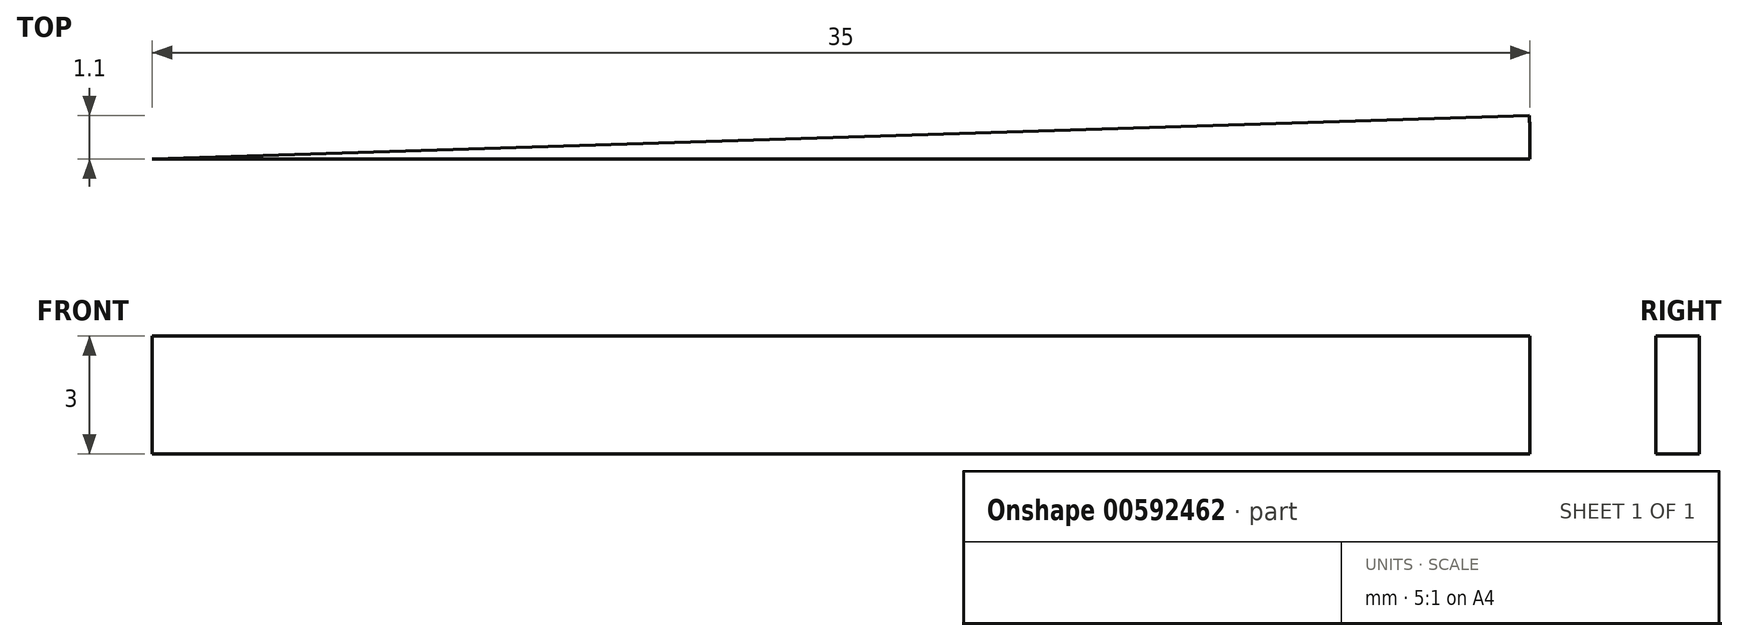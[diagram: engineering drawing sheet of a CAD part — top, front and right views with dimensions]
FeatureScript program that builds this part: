
annotation { "Feature Type Name" : "Feature", "Feature Type Description" : "" }
export const myFeature = defineFeature(function(context is Context, id is Id, definition is map)
    precondition{}
    {
        {
            var Q0;
            Q0=qCreatedBy(makeId("Top.planeOp"),FACE);
            var sketch = newSketch(context, id + "F0", { "sketchPlane" : qUnion([Q0])});
            skCircle(sketch, "E0", {"center": v(0, 0) * mm, "radius": 35 * mm});
            skLineSegment(sketch, "E1", {"start": v(0, 0) * mm, "end": v(35, 0) * mm});
            skLineSegment(sketch, "E2.1.0", {"start": v(0, 0) * mm, "end": v(34.98, 1.1) * mm});
            skLineSegment(sketch, "E3.1.2.0", {"start": v(0, 0) * mm, "end": v(34.93, 2.2) * mm});
            skLineSegment(sketch, "E3.1.3.0", {"start": v(0, 0) * mm, "end": v(34.84, 3.3) * mm});
            skLineSegment(sketch, "E3.1.4.0", {"start": v(0, 0) * mm, "end": v(34.72, 4.39) * mm});
            skLineSegment(sketch, "E3.1.5.0", {"start": v(0, 0) * mm, "end": v(34.57, 5.48) * mm});
            skLineSegment(sketch, "E3.1.6.0", {"start": v(0, 0) * mm, "end": v(34.38, 6.56) * mm});
            skLineSegment(sketch, "E4.1.7.0", {"start": v(0, 0) * mm, "end": v(34.16, 7.64) * mm});
            skLineSegment(sketch, "E5.1.8.0", {"start": v(0, 0) * mm, "end": v(33.9, 8.7) * mm});
            skLineSegment(sketch, "E6.1.9.0", {"start": v(0, 0) * mm, "end": v(33.61, 9.76) * mm});
            skLineSegment(sketch, "E7.1.10.0", {"start": v(0, 0) * mm, "end": v(33.29, 10.82) * mm});
            skLineSegment(sketch, "E8.1.11.0", {"start": v(0, 0) * mm, "end": v(32.93, 11.86) * mm});
            skLineSegment(sketch, "E9.1.12.0", {"start": v(0, 0) * mm, "end": v(32.54, 12.88) * mm});
            skLineSegment(sketch, "E9.1.13.0", {"start": v(0, 0) * mm, "end": v(32.12, 13.9) * mm});
            skLineSegment(sketch, "E9.1.14.0", {"start": v(0, 0) * mm, "end": v(31.67, 14.9) * mm});
            skLineSegment(sketch, "E9.1.15.0", {"start": v(0, 0) * mm, "end": v(31.19, 15.89) * mm});
            skLineSegment(sketch, "E9.1.16.0", {"start": v(0, 0) * mm, "end": v(30.67, 16.86) * mm});
            skLineSegment(sketch, "E9.1.17.0", {"start": v(0, 0) * mm, "end": v(30.13, 17.82) * mm});
            skLineSegment(sketch, "E9.1.18.0", {"start": v(0, 0) * mm, "end": v(29.55, 18.75) * mm});
            skLineSegment(sketch, "E9.1.19.0", {"start": v(0, 0) * mm, "end": v(28.95, 19.67) * mm});
            skLineSegment(sketch, "E9.1.20.0", {"start": v(0, 0) * mm, "end": v(28.32, 20.57) * mm});
            skLineSegment(sketch, "E9.1.21.0", {"start": v(0, 0) * mm, "end": v(27.66, 21.45) * mm});
            skLineSegment(sketch, "E9.1.22.0", {"start": v(0, 0) * mm, "end": v(26.97, 22.3) * mm});
            skLineSegment(sketch, "E9.1.23.0", {"start": v(0, 0) * mm, "end": v(26.25, 23.15) * mm});
            skLineSegment(sketch, "E9.1.24.0", {"start": v(0, 0) * mm, "end": v(25.51, 23.96) * mm});
            skLineSegment(sketch, "E9.1.25.0", {"start": v(0, 0) * mm, "end": v(24.75, 24.75) * mm});
            skLineSegment(sketch, "E9.1.26.0", {"start": v(0, 0) * mm, "end": v(23.96, 25.51) * mm});
            skLineSegment(sketch, "E9.1.27.0", {"start": v(0, 0) * mm, "end": v(23.15, 26.25) * mm});
            skLineSegment(sketch, "E9.1.28.0", {"start": v(0, 0) * mm, "end": v(22.3, 26.97) * mm});
            skLineSegment(sketch, "E9.1.29.0", {"start": v(0, 0) * mm, "end": v(21.45, 27.66) * mm});
            skLineSegment(sketch, "E9.1.30.0", {"start": v(0, 0) * mm, "end": v(20.57, 28.32) * mm});
            skLineSegment(sketch, "E9.1.31.0", {"start": v(0, 0) * mm, "end": v(19.67, 28.95) * mm});
            skLineSegment(sketch, "E9.1.32.0", {"start": v(0, 0) * mm, "end": v(18.75, 29.55) * mm});
            skLineSegment(sketch, "E9.1.33.0", {"start": v(0, 0) * mm, "end": v(17.82, 30.13) * mm});
            skLineSegment(sketch, "E9.1.34.0", {"start": v(0, 0) * mm, "end": v(16.86, 30.67) * mm});
            skLineSegment(sketch, "E9.1.35.0", {"start": v(0, 0) * mm, "end": v(15.89, 31.19) * mm});
            skLineSegment(sketch, "E9.1.36.0", {"start": v(0, 0) * mm, "end": v(14.9, 31.67) * mm});
            skLineSegment(sketch, "E9.1.37.0", {"start": v(0, 0) * mm, "end": v(13.9, 32.12) * mm});
            skLineSegment(sketch, "E9.1.38.0", {"start": v(0, 0) * mm, "end": v(12.88, 32.54) * mm});
            skLineSegment(sketch, "E9.1.39.0", {"start": v(0, 0) * mm, "end": v(11.86, 32.93) * mm});
            skLineSegment(sketch, "E9.1.40.0", {"start": v(0, 0) * mm, "end": v(10.82, 33.29) * mm});
            skLineSegment(sketch, "E9.1.41.0", {"start": v(0, 0) * mm, "end": v(9.76, 33.61) * mm});
            skLineSegment(sketch, "E9.1.42.0", {"start": v(0, 0) * mm, "end": v(8.7, 33.9) * mm});
            skLineSegment(sketch, "E9.1.43.0", {"start": v(0, 0) * mm, "end": v(7.64, 34.16) * mm});
            skLineSegment(sketch, "E9.1.44.0", {"start": v(0, 0) * mm, "end": v(6.56, 34.38) * mm});
            skLineSegment(sketch, "E9.1.45.0", {"start": v(0, 0) * mm, "end": v(5.48, 34.57) * mm});
            skLineSegment(sketch, "E9.1.46.0", {"start": v(0, 0) * mm, "end": v(4.39, 34.72) * mm});
            skLineSegment(sketch, "E9.1.47.0", {"start": v(0, 0) * mm, "end": v(3.3, 34.84) * mm});
            skLineSegment(sketch, "E9.1.48.0", {"start": v(0, 0) * mm, "end": v(2.2, 34.93) * mm});
            skLineSegment(sketch, "E9.1.49.0", {"start": v(0, 0) * mm, "end": v(1.1, 34.98) * mm});
            skLineSegment(sketch, "E9.1.50.0", {"start": v(0, 0) * mm, "end": v(0, 35) * mm});
            skLineSegment(sketch, "E9.1.51.0", {"start": v(0, 0) * mm, "end": v(-1.1, 34.98) * mm});
            skLineSegment(sketch, "E9.1.52.0", {"start": v(0, 0) * mm, "end": v(-2.2, 34.93) * mm});
            skLineSegment(sketch, "E9.1.53.0", {"start": v(0, 0) * mm, "end": v(-3.3, 34.84) * mm});
            skLineSegment(sketch, "E9.1.54.0", {"start": v(0, 0) * mm, "end": v(-4.39, 34.72) * mm});
            skLineSegment(sketch, "E9.1.55.0", {"start": v(0, 0) * mm, "end": v(-5.48, 34.57) * mm});
            skLineSegment(sketch, "E9.1.56.0", {"start": v(0, 0) * mm, "end": v(-6.56, 34.38) * mm});
            skLineSegment(sketch, "E9.1.57.0", {"start": v(0, 0) * mm, "end": v(-7.64, 34.16) * mm});
            skLineSegment(sketch, "E9.1.58.0", {"start": v(0, 0) * mm, "end": v(-8.7, 33.9) * mm});
            skLineSegment(sketch, "E9.1.59.0", {"start": v(0, 0) * mm, "end": v(-9.76, 33.61) * mm});
            skLineSegment(sketch, "E9.1.60.0", {"start": v(0, 0) * mm, "end": v(-10.82, 33.29) * mm});
            skLineSegment(sketch, "E9.1.61.0", {"start": v(0, 0) * mm, "end": v(-11.86, 32.93) * mm});
            skLineSegment(sketch, "E9.1.62.0", {"start": v(0, 0) * mm, "end": v(-12.88, 32.54) * mm});
            skLineSegment(sketch, "E9.1.63.0", {"start": v(0, 0) * mm, "end": v(-13.9, 32.12) * mm});
            skLineSegment(sketch, "E9.1.64.0", {"start": v(0, 0) * mm, "end": v(-14.9, 31.67) * mm});
            skLineSegment(sketch, "E9.1.65.0", {"start": v(0, 0) * mm, "end": v(-15.89, 31.19) * mm});
            skLineSegment(sketch, "E9.1.66.0", {"start": v(0, 0) * mm, "end": v(-16.86, 30.67) * mm});
            skLineSegment(sketch, "E9.1.67.0", {"start": v(0, 0) * mm, "end": v(-17.82, 30.13) * mm});
            skLineSegment(sketch, "E9.1.68.0", {"start": v(0, 0) * mm, "end": v(-18.75, 29.55) * mm});
            skLineSegment(sketch, "E9.1.69.0", {"start": v(0, 0) * mm, "end": v(-19.67, 28.95) * mm});
            skLineSegment(sketch, "E9.1.70.0", {"start": v(0, 0) * mm, "end": v(-20.57, 28.32) * mm});
            skLineSegment(sketch, "E9.1.71.0", {"start": v(0, 0) * mm, "end": v(-21.45, 27.66) * mm});
            skLineSegment(sketch, "E9.1.72.0", {"start": v(0, 0) * mm, "end": v(-22.3, 26.97) * mm});
            skLineSegment(sketch, "E9.1.73.0", {"start": v(0, 0) * mm, "end": v(-23.15, 26.25) * mm});
            skLineSegment(sketch, "E9.1.74.0", {"start": v(0, 0) * mm, "end": v(-23.96, 25.51) * mm});
            skLineSegment(sketch, "E9.1.75.0", {"start": v(0, 0) * mm, "end": v(-24.75, 24.75) * mm});
            skLineSegment(sketch, "E9.1.76.0", {"start": v(0, 0) * mm, "end": v(-25.51, 23.96) * mm});
            skLineSegment(sketch, "E9.1.77.0", {"start": v(0, 0) * mm, "end": v(-26.25, 23.15) * mm});
            skLineSegment(sketch, "E9.1.78.0", {"start": v(0, 0) * mm, "end": v(-26.97, 22.3) * mm});
            skLineSegment(sketch, "E9.1.79.0", {"start": v(0, 0) * mm, "end": v(-27.66, 21.45) * mm});
            skLineSegment(sketch, "E9.1.80.0", {"start": v(0, 0) * mm, "end": v(-28.32, 20.57) * mm});
            skLineSegment(sketch, "E9.1.81.0", {"start": v(0, 0) * mm, "end": v(-28.95, 19.67) * mm});
            skLineSegment(sketch, "E9.1.82.0", {"start": v(0, 0) * mm, "end": v(-29.55, 18.75) * mm});
            skLineSegment(sketch, "E9.1.83.0", {"start": v(0, 0) * mm, "end": v(-30.13, 17.82) * mm});
            skLineSegment(sketch, "E9.1.84.0", {"start": v(0, 0) * mm, "end": v(-30.67, 16.86) * mm});
            skLineSegment(sketch, "E9.1.85.0", {"start": v(0, 0) * mm, "end": v(-31.19, 15.89) * mm});
            skLineSegment(sketch, "E9.1.86.0", {"start": v(0, 0) * mm, "end": v(-31.67, 14.9) * mm});
            skLineSegment(sketch, "E9.1.87.0", {"start": v(0, 0) * mm, "end": v(-32.12, 13.9) * mm});
            skLineSegment(sketch, "E9.1.88.0", {"start": v(0, 0) * mm, "end": v(-32.54, 12.88) * mm});
            skLineSegment(sketch, "E9.1.89.0", {"start": v(0, 0) * mm, "end": v(-32.93, 11.86) * mm});
            skLineSegment(sketch, "E9.1.90.0", {"start": v(0, 0) * mm, "end": v(-33.29, 10.82) * mm});
            skLineSegment(sketch, "E9.1.91.0", {"start": v(0, 0) * mm, "end": v(-33.61, 9.76) * mm});
            skLineSegment(sketch, "E9.1.92.0", {"start": v(0, 0) * mm, "end": v(-33.9, 8.7) * mm});
            skLineSegment(sketch, "E9.1.93.0", {"start": v(0, 0) * mm, "end": v(-34.16, 7.64) * mm});
            skLineSegment(sketch, "E9.1.94.0", {"start": v(0, 0) * mm, "end": v(-34.38, 6.56) * mm});
            skLineSegment(sketch, "E9.1.95.0", {"start": v(0, 0) * mm, "end": v(-34.57, 5.48) * mm});
            skLineSegment(sketch, "E9.1.96.0", {"start": v(0, 0) * mm, "end": v(-34.72, 4.39) * mm});
            skLineSegment(sketch, "E9.1.97.0", {"start": v(0, 0) * mm, "end": v(-34.84, 3.3) * mm});
            skLineSegment(sketch, "E9.1.98.0", {"start": v(0, 0) * mm, "end": v(-34.93, 2.2) * mm});
            skLineSegment(sketch, "E9.1.99.0", {"start": v(0, 0) * mm, "end": v(-34.98, 1.1) * mm});
            skLineSegment(sketch, "E9.1.100.0", {"start": v(0, 0) * mm, "end": v(-35, 0) * mm});
            skLineSegment(sketch, "E9.1.101.0", {"start": v(0, 0) * mm, "end": v(-34.98, -1.1) * mm});
            skLineSegment(sketch, "E9.1.102.0", {"start": v(0, 0) * mm, "end": v(-34.93, -2.2) * mm});
            skLineSegment(sketch, "E9.1.103.0", {"start": v(0, 0) * mm, "end": v(-34.84, -3.3) * mm});
            skLineSegment(sketch, "E9.1.104.0", {"start": v(0, 0) * mm, "end": v(-34.72, -4.39) * mm});
            skLineSegment(sketch, "E9.1.105.0", {"start": v(0, 0) * mm, "end": v(-34.57, -5.48) * mm});
            skLineSegment(sketch, "E9.1.106.0", {"start": v(0, 0) * mm, "end": v(-34.38, -6.56) * mm});
            skLineSegment(sketch, "E9.1.107.0", {"start": v(0, 0) * mm, "end": v(-34.16, -7.64) * mm});
            skLineSegment(sketch, "E9.1.108.0", {"start": v(0, 0) * mm, "end": v(-33.9, -8.7) * mm});
            skLineSegment(sketch, "E9.1.109.0", {"start": v(0, 0) * mm, "end": v(-33.61, -9.76) * mm});
            skLineSegment(sketch, "E9.1.110.0", {"start": v(0, 0) * mm, "end": v(-33.29, -10.82) * mm});
            skLineSegment(sketch, "E9.1.111.0", {"start": v(0, 0) * mm, "end": v(-32.93, -11.86) * mm});
            skLineSegment(sketch, "E9.1.112.0", {"start": v(0, 0) * mm, "end": v(-32.54, -12.88) * mm});
            skLineSegment(sketch, "E9.1.113.0", {"start": v(0, 0) * mm, "end": v(-32.12, -13.9) * mm});
            skLineSegment(sketch, "E9.1.114.0", {"start": v(0, 0) * mm, "end": v(-31.67, -14.9) * mm});
            skLineSegment(sketch, "E9.1.115.0", {"start": v(0, 0) * mm, "end": v(-31.19, -15.89) * mm});
            skLineSegment(sketch, "E9.1.116.0", {"start": v(0, 0) * mm, "end": v(-30.67, -16.86) * mm});
            skLineSegment(sketch, "E9.1.117.0", {"start": v(0, 0) * mm, "end": v(-30.13, -17.82) * mm});
            skLineSegment(sketch, "E9.1.118.0", {"start": v(0, 0) * mm, "end": v(-29.55, -18.75) * mm});
            skLineSegment(sketch, "E9.1.119.0", {"start": v(0, 0) * mm, "end": v(-28.95, -19.67) * mm});
            skLineSegment(sketch, "E9.1.120.0", {"start": v(0, 0) * mm, "end": v(-28.32, -20.57) * mm});
            skLineSegment(sketch, "E9.1.121.0", {"start": v(0, 0) * mm, "end": v(-27.66, -21.45) * mm});
            skLineSegment(sketch, "E9.1.122.0", {"start": v(0, 0) * mm, "end": v(-26.97, -22.3) * mm});
            skLineSegment(sketch, "E9.1.123.0", {"start": v(0, 0) * mm, "end": v(-26.25, -23.15) * mm});
            skLineSegment(sketch, "E9.1.124.0", {"start": v(0, 0) * mm, "end": v(-25.51, -23.96) * mm});
            skLineSegment(sketch, "E9.1.125.0", {"start": v(0, 0) * mm, "end": v(-24.75, -24.75) * mm});
            skLineSegment(sketch, "E9.1.126.0", {"start": v(0, 0) * mm, "end": v(-23.96, -25.51) * mm});
            skLineSegment(sketch, "E9.1.127.0", {"start": v(0, 0) * mm, "end": v(-23.15, -26.25) * mm});
            skLineSegment(sketch, "E9.1.128.0", {"start": v(0, 0) * mm, "end": v(-22.3, -26.97) * mm});
            skLineSegment(sketch, "E9.1.129.0", {"start": v(0, 0) * mm, "end": v(-21.45, -27.66) * mm});
            skLineSegment(sketch, "E9.1.130.0", {"start": v(0, 0) * mm, "end": v(-20.57, -28.32) * mm});
            skLineSegment(sketch, "E9.1.131.0", {"start": v(0, 0) * mm, "end": v(-19.67, -28.95) * mm});
            skLineSegment(sketch, "E9.1.132.0", {"start": v(0, 0) * mm, "end": v(-18.75, -29.55) * mm});
            skLineSegment(sketch, "E9.1.133.0", {"start": v(0, 0) * mm, "end": v(-17.82, -30.13) * mm});
            skLineSegment(sketch, "E9.1.134.0", {"start": v(0, 0) * mm, "end": v(-16.86, -30.67) * mm});
            skLineSegment(sketch, "E9.1.135.0", {"start": v(0, 0) * mm, "end": v(-15.89, -31.19) * mm});
            skLineSegment(sketch, "E9.1.136.0", {"start": v(0, 0) * mm, "end": v(-14.9, -31.67) * mm});
            skLineSegment(sketch, "E9.1.137.0", {"start": v(0, 0) * mm, "end": v(-13.9, -32.12) * mm});
            skLineSegment(sketch, "E9.1.138.0", {"start": v(0, 0) * mm, "end": v(-12.88, -32.54) * mm});
            skLineSegment(sketch, "E9.1.139.0", {"start": v(0, 0) * mm, "end": v(-11.86, -32.93) * mm});
            skLineSegment(sketch, "E9.1.140.0", {"start": v(0, 0) * mm, "end": v(-10.82, -33.29) * mm});
            skLineSegment(sketch, "E9.1.141.0", {"start": v(0, 0) * mm, "end": v(-9.76, -33.61) * mm});
            skLineSegment(sketch, "E9.1.142.0", {"start": v(0, 0) * mm, "end": v(-8.7, -33.9) * mm});
            skLineSegment(sketch, "E9.1.143.0", {"start": v(0, 0) * mm, "end": v(-7.64, -34.16) * mm});
            skLineSegment(sketch, "E9.1.144.0", {"start": v(0, 0) * mm, "end": v(-6.56, -34.38) * mm});
            skLineSegment(sketch, "E9.1.145.0", {"start": v(0, 0) * mm, "end": v(-5.48, -34.57) * mm});
            skLineSegment(sketch, "E9.1.146.0", {"start": v(0, 0) * mm, "end": v(-4.39, -34.72) * mm});
            skLineSegment(sketch, "E9.1.147.0", {"start": v(0, 0) * mm, "end": v(-3.3, -34.84) * mm});
            skLineSegment(sketch, "E9.1.148.0", {"start": v(0, 0) * mm, "end": v(-2.2, -34.93) * mm});
            skLineSegment(sketch, "E9.1.149.0", {"start": v(0, 0) * mm, "end": v(-1.1, -34.98) * mm});
            skLineSegment(sketch, "E9.1.150.0", {"start": v(0, 0) * mm, "end": v(0, -35) * mm});
            skLineSegment(sketch, "E9.1.151.0", {"start": v(0, 0) * mm, "end": v(1.1, -34.98) * mm});
            skLineSegment(sketch, "E9.1.152.0", {"start": v(0, 0) * mm, "end": v(2.2, -34.93) * mm});
            skLineSegment(sketch, "E9.1.153.0", {"start": v(0, 0) * mm, "end": v(3.3, -34.84) * mm});
            skLineSegment(sketch, "E9.1.154.0", {"start": v(0, 0) * mm, "end": v(4.39, -34.72) * mm});
            skLineSegment(sketch, "E9.1.155.0", {"start": v(0, 0) * mm, "end": v(5.48, -34.57) * mm});
            skLineSegment(sketch, "E9.1.156.0", {"start": v(0, 0) * mm, "end": v(6.56, -34.38) * mm});
            skLineSegment(sketch, "E9.1.157.0", {"start": v(0, 0) * mm, "end": v(7.64, -34.16) * mm});
            skLineSegment(sketch, "E9.1.158.0", {"start": v(0, 0) * mm, "end": v(8.7, -33.9) * mm});
            skLineSegment(sketch, "E9.1.159.0", {"start": v(0, 0) * mm, "end": v(9.76, -33.61) * mm});
            skLineSegment(sketch, "E9.1.160.0", {"start": v(0, 0) * mm, "end": v(10.82, -33.29) * mm});
            skLineSegment(sketch, "E9.1.161.0", {"start": v(0, 0) * mm, "end": v(11.86, -32.93) * mm});
            skLineSegment(sketch, "E9.1.162.0", {"start": v(0, 0) * mm, "end": v(12.88, -32.54) * mm});
            skLineSegment(sketch, "E9.1.163.0", {"start": v(0, 0) * mm, "end": v(13.9, -32.12) * mm});
            skLineSegment(sketch, "E9.1.164.0", {"start": v(0, 0) * mm, "end": v(14.9, -31.67) * mm});
            skLineSegment(sketch, "E9.1.165.0", {"start": v(0, 0) * mm, "end": v(15.89, -31.19) * mm});
            skLineSegment(sketch, "E9.1.166.0", {"start": v(0, 0) * mm, "end": v(16.86, -30.67) * mm});
            skLineSegment(sketch, "E9.1.167.0", {"start": v(0, 0) * mm, "end": v(17.82, -30.13) * mm});
            skLineSegment(sketch, "E9.1.168.0", {"start": v(0, 0) * mm, "end": v(18.75, -29.55) * mm});
            skLineSegment(sketch, "E9.1.169.0", {"start": v(0, 0) * mm, "end": v(19.67, -28.95) * mm});
            skLineSegment(sketch, "E9.1.170.0", {"start": v(0, 0) * mm, "end": v(20.57, -28.32) * mm});
            skLineSegment(sketch, "E9.1.171.0", {"start": v(0, 0) * mm, "end": v(21.45, -27.66) * mm});
            skLineSegment(sketch, "E9.1.172.0", {"start": v(0, 0) * mm, "end": v(22.3, -26.97) * mm});
            skLineSegment(sketch, "E9.1.173.0", {"start": v(0, 0) * mm, "end": v(23.15, -26.25) * mm});
            skLineSegment(sketch, "E9.1.174.0", {"start": v(0, 0) * mm, "end": v(23.96, -25.51) * mm});
            skLineSegment(sketch, "E9.1.175.0", {"start": v(0, 0) * mm, "end": v(24.75, -24.75) * mm});
            skLineSegment(sketch, "E9.1.176.0", {"start": v(0, 0) * mm, "end": v(25.51, -23.96) * mm});
            skLineSegment(sketch, "E9.1.177.0", {"start": v(0, 0) * mm, "end": v(26.25, -23.15) * mm});
            skLineSegment(sketch, "E9.1.178.0", {"start": v(0, 0) * mm, "end": v(26.97, -22.3) * mm});
            skLineSegment(sketch, "E9.1.179.0", {"start": v(0, 0) * mm, "end": v(27.66, -21.45) * mm});
            skLineSegment(sketch, "E9.1.180.0", {"start": v(0, 0) * mm, "end": v(28.32, -20.57) * mm});
            skLineSegment(sketch, "E9.1.181.0", {"start": v(0, 0) * mm, "end": v(28.95, -19.67) * mm});
            skLineSegment(sketch, "E9.1.182.0", {"start": v(0, 0) * mm, "end": v(29.55, -18.75) * mm});
            skLineSegment(sketch, "E9.1.183.0", {"start": v(0, 0) * mm, "end": v(30.13, -17.82) * mm});
            skLineSegment(sketch, "E9.1.184.0", {"start": v(0, 0) * mm, "end": v(30.67, -16.86) * mm});
            skLineSegment(sketch, "E9.1.185.0", {"start": v(0, 0) * mm, "end": v(31.19, -15.89) * mm});
            skLineSegment(sketch, "E9.1.186.0", {"start": v(0, 0) * mm, "end": v(31.67, -14.9) * mm});
            skLineSegment(sketch, "E9.1.187.0", {"start": v(0, 0) * mm, "end": v(32.12, -13.9) * mm});
            skLineSegment(sketch, "E9.1.188.0", {"start": v(0, 0) * mm, "end": v(32.54, -12.88) * mm});
            skLineSegment(sketch, "E9.1.189.0", {"start": v(0, 0) * mm, "end": v(32.93, -11.86) * mm});
            skLineSegment(sketch, "E9.1.190.0", {"start": v(0, 0) * mm, "end": v(33.29, -10.82) * mm});
            skLineSegment(sketch, "E9.1.191.0", {"start": v(0, 0) * mm, "end": v(33.61, -9.76) * mm});
            skLineSegment(sketch, "E9.1.192.0", {"start": v(0, 0) * mm, "end": v(33.9, -8.7) * mm});
            skLineSegment(sketch, "E9.1.193.0", {"start": v(0, 0) * mm, "end": v(34.16, -7.64) * mm});
            skLineSegment(sketch, "E9.1.194.0", {"start": v(0, 0) * mm, "end": v(34.38, -6.56) * mm});
            skLineSegment(sketch, "E9.1.195.0", {"start": v(0, 0) * mm, "end": v(34.57, -5.48) * mm});
            skLineSegment(sketch, "E9.1.196.0", {"start": v(0, 0) * mm, "end": v(34.72, -4.39) * mm});
            skLineSegment(sketch, "E9.1.197.0", {"start": v(0, 0) * mm, "end": v(34.84, -3.3) * mm});
            skLineSegment(sketch, "E9.1.198.0", {"start": v(0, 0) * mm, "end": v(34.93, -2.2) * mm});
            skLineSegment(sketch, "E9.1.199.0", {"start": v(0, 0) * mm, "end": v(34.98, -1.1) * mm});
            skSolve(sketch);
        }
        {
            var Q0;
            {var subQ0=sQuery(id+"F0.wireOp",EDGE,"E1");Q0=makeQuery(id+"F0.imprint","IMPRINT",FACE,{"disambiguationData":[TD([[makeQuery(id+"F0.imprint","IMPRINT",EDGE,{"derivedFrom":subQ0}),1.0]])]});}
            extrude(context, id + "F1", {"entities" : qUnion([Q0]), "depth" : 3 * mm, "offsetDistance" : 25 * mm});
        }
    });
